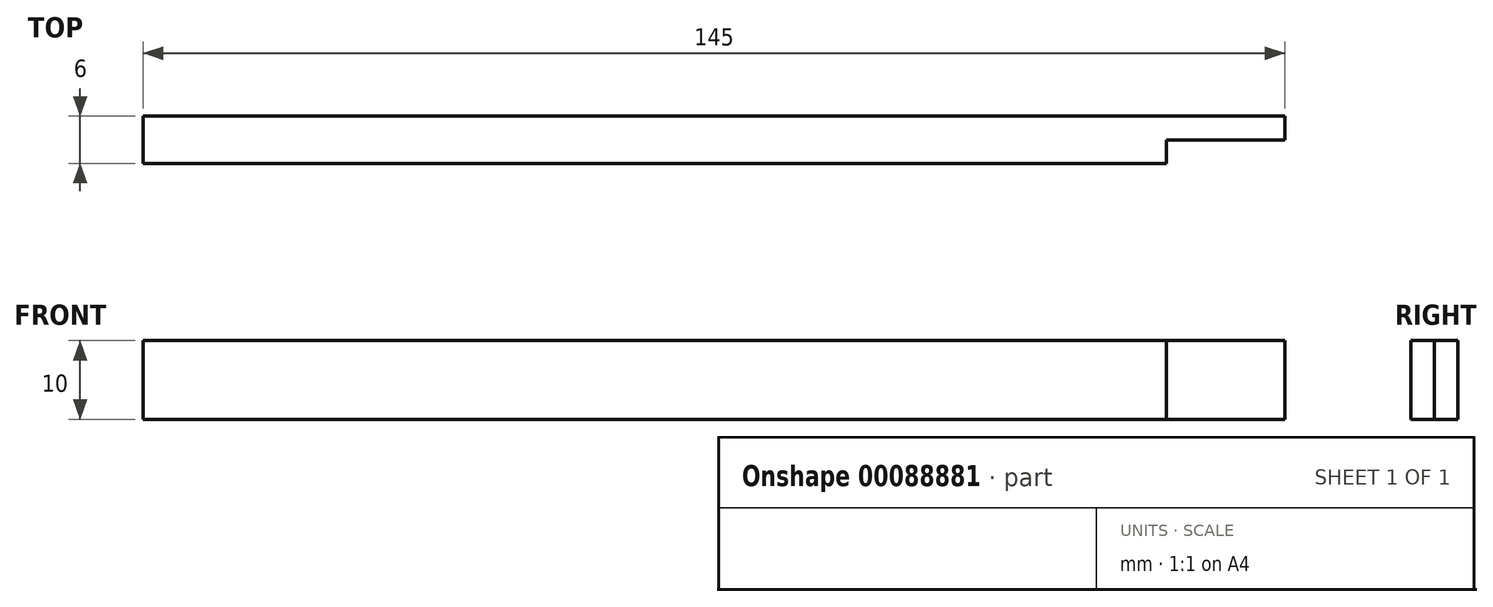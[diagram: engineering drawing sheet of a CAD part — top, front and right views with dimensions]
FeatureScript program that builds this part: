
annotation { "Feature Type Name" : "Feature", "Feature Type Description" : "" }
export const myFeature = defineFeature(function(context is Context, id is Id, definition is map)
    precondition{}
    {
        {
            var Q0;
            Q0=qCreatedBy(makeId("Top.planeOp"),FACE);
            var sketch = newSketch(context, id + "F0", { "sketchPlane" : qUnion([Q0])});
            skLineSegment(sketch, "E0.bottom", {"start": v(72.5, -3) * mm, "end": v(-72.5, -3) * mm});
            skLineSegment(sketch, "E0.top", {"start": v(72.5, 3) * mm, "end": v(-72.5, 3) * mm});
            skLineSegment(sketch, "E0.left", {"start": v(72.5, -3) * mm, "end": v(72.5, 3) * mm});
            skLineSegment(sketch, "E0.right", {"start": v(-72.5, -3) * mm, "end": v(-72.5, 3) * mm});
            skPoint(sketch, "E0.middle", {"position": v(0, 0) * mm});
            skSolve(sketch);
        }
        {
            var Q0;
            Q0 = qSketchRegion(id + "F0", true);
            extrude(context, id + "F1", {"entities" : qUnion([Q0]), "depth" : 10 * mm});
        }
        {
            var Q0;
            Q0=makeQuery(id+"F1.opExtrude","SWEPT_FACE",FACE,{"disambiguationData":[OSD([sQuery(id+"F0.wireOp",EDGE,"E0.bottom")])]});
            var sketch = newSketch(context, id + "F2", { "sketchPlane" : qUnion([Q0])});
            skLineSegment(sketch, "E1.bottom", {"start": v(72.5, 10) * mm, "end": v(57.5, 10) * mm});
            skLineSegment(sketch, "E1.top", {"start": v(72.5, 0) * mm, "end": v(57.5, 0) * mm});
            skLineSegment(sketch, "E1.left", {"start": v(72.5, 10) * mm, "end": v(72.5, 0) * mm});
            skLineSegment(sketch, "E1.right", {"start": v(57.5, 10) * mm, "end": v(57.5, 0) * mm});
            skSolve(sketch);
        }
        {
            var Q0;
            Q0 = qSketchRegion(id + "F2", true);
            extrude(context, id + "F3", {"entities" : qUnion([Q0]), "operationType" : NewBodyOperationType.REMOVE, "oppositeDirection" : true, "depth" : 3 * mm});
        }
    });
